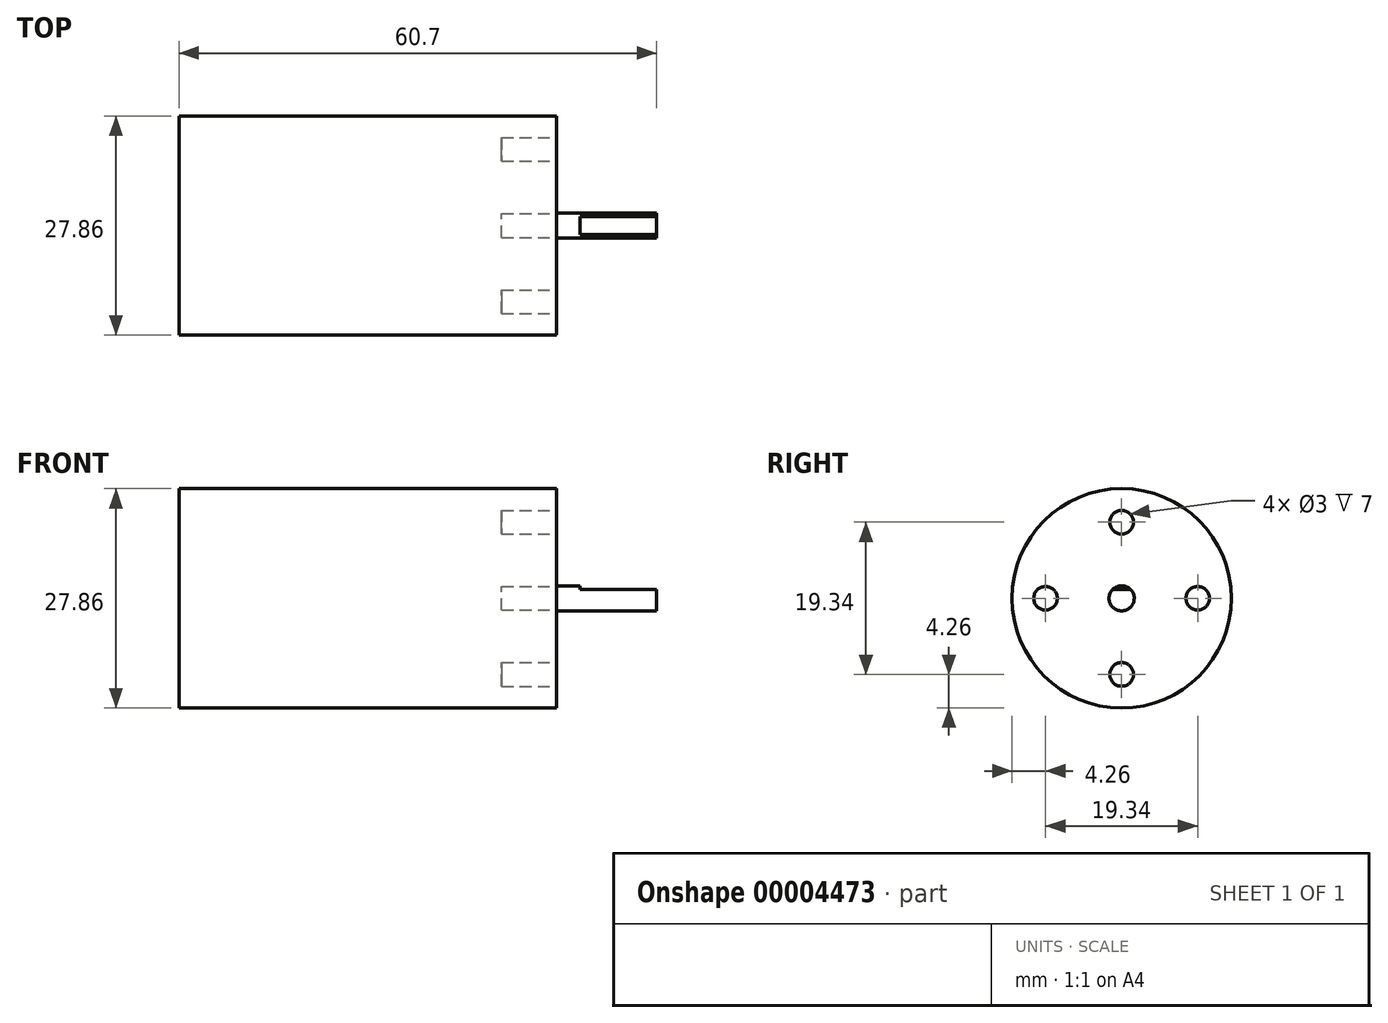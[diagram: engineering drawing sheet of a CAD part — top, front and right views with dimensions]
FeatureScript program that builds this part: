
annotation { "Feature Type Name" : "Feature", "Feature Type Description" : "" }
export const myFeature = defineFeature(function(context is Context, id is Id, definition is map)
    precondition{}
    {
        {
            var Q0;
            Q0=qCreatedBy(makeId("Front.planeOp"),FACE);
            var sketch = newSketch(context, id + "F0", { "sketchPlane" : qUnion([Q0])});
            skLineSegment(sketch, "E0", {"start": v(-48, 0) * mm, "end": v(-48, 13.93) * mm});
            skLineSegment(sketch, "E1", {"start": v(-48, 13.93) * mm, "end": v(0, 13.93) * mm});
            skLineSegment(sketch, "E2", {"start": v(0, 13.93) * mm, "end": v(0, 0) * mm});
            skLineSegment(sketch, "E3", {"start": v(0, 1.6) * mm, "end": v(12.7, 1.6) * mm});
            skLineSegment(sketch, "E4", {"start": v(12.7, 1.6) * mm, "end": v(12.7, 0) * mm});
            skLineSegment(sketch, "E5", {"start": v(2.98, 1.6) * mm, "end": v(2.98, 1.12) * mm});
            skLineSegment(sketch, "E6", {"start": v(2.98, 1.12) * mm, "end": v(12.7, 1.12) * mm});
            skLineSegment(sketch, "E7", {"start": v(-62.12, 0) * mm, "end": v(33.72, 0) * mm, "construction": true});
            skLineSegment(sketch, "E8", {"start": v(-48, 0) * mm, "end": v(12.7, 0) * mm});
            skSolve(sketch);
        }
        {
            var Q0;
            Q0=qCreatedBy(makeId("Right.planeOp"),FACE);
            var sketch = newSketch(context, id + "F1", { "sketchPlane" : qUnion([Q0])});
            skLineSegment(sketch, "E9", {"start": v(0, 0) * mm, "end": v(9.67, 0) * mm});
            skCircle(sketch, "E10", {"center": v(9.67, 0) * mm, "radius": 1.5 * mm});
            skSolve(sketch);
        }
        {
            var Q0;
            {var subQ3=sQuery(id+"F0.wireOp",EDGE,"E0");Q0=makeQuery(id+"F0.imprint","IMPRINT",FACE,{"disambiguationData":[TD([[makeQuery(id+"F0.imprint","IMPRINT",EDGE,{"derivedFrom":subQ3}),-1.0]])]});}
            var Q1;
            {var subQ6=sQuery(id+"F0.wireOp",EDGE,"E5");Q1=makeQuery(id+"F0.imprint","IMPRINT",FACE,{"disambiguationData":[TD([[makeQuery(id+"F0.imprint","IMPRINT",EDGE,{"derivedFrom":subQ6}),-1.0]])]});}
            var Q2;
            {var subQ1=sQuery(id+"F0.wireOp",EDGE,"E5");Q2=makeQuery(id+"F0.imprint","IMPRINT",FACE,{"disambiguationData":[TD([[makeQuery(id+"F0.imprint","IMPRINT",EDGE,{"derivedFrom":subQ1}),1.0]])]});}
            var Q3;
            Q3=sQuery(id+"F0.wireOp",EDGE,"E7");
            revolve(context, id + "F2", {"entities" : qUnion([Q0, Q1, Q2]), "axis" : qUnion([Q3]), "revolveType" : RevolveType.FULL});
        }
        {
            var Q0;
            {var subQ1=sQuery(id+"F0.wireOp",EDGE,"E5");Q0=makeQuery(id+"F0.imprint","IMPRINT",FACE,{"disambiguationData":[TD([[makeQuery(id+"F0.imprint","IMPRINT",EDGE,{"derivedFrom":subQ1}),1.0]])]});}
            extrude(context, id + "F3", {"entities" : qUnion([Q0]), "operationType" : NewBodyOperationType.REMOVE, "endBound" : BoundingType.SYMMETRIC, "oppositeDirection" : true, "depth" : 10 * mm});
        }
        {
            var Q0;
            {var subQ0=sQuery(id+"F1.wireOp",EDGE,"E10");Q0=makeQuery(id+"F1.imprint","IMPRINT",FACE,{"disambiguationData":[TD([[makeQuery(id+"F1.imprint","IMPRINT",EDGE,{"derivedFrom":subQ0}),1.0]])]});}
            extrude(context, id + "F4", {"entities" : qUnion([Q0]), "oppositeDirection" : true, "depth" : 7 * mm});
        }
        {
            var Q0;
            Q0=makeQuery(id+"F4.opExtrude","SWEPT_BODY",BODY,{"disambiguationData":[OSD([sQuery(id+"F1.wireOp",EDGE,"E10")])]});
            var Q1;
            Q1=sQuery(id+"F0.wireOp",EDGE,"E7");
            circularPattern(context, id + "F5", {"entities" : qUnion([Q0]), "axis" : qUnion([Q1]), "angle" : 90 * degree, "instanceCount" : 4});
        }
        {
            var Q0;
            Q0=makeQuery(id+"F5.opPattern","COPY",BODY,{"derivedFrom":makeQuery(id+"F4.opExtrude","SWEPT_BODY",BODY,{"disambiguationData":[OSD([sQuery(id+"F1.wireOp",EDGE,"E10")])]}),"instanceName":"2"});
            var Q1;
            Q1=makeQuery(id+"F4.opExtrude","SWEPT_BODY",BODY,{"disambiguationData":[OSD([sQuery(id+"F1.wireOp",EDGE,"E10")])]});
            var Q2;
            Q2=makeQuery(id+"F5.opPattern","COPY",BODY,{"derivedFrom":makeQuery(id+"F4.opExtrude","SWEPT_BODY",BODY,{"disambiguationData":[OSD([sQuery(id+"F1.wireOp",EDGE,"E10")])]}),"instanceName":"1"});
            var Q3;
            Q3=makeQuery(id+"F5.opPattern","COPY",BODY,{"derivedFrom":makeQuery(id+"F4.opExtrude","SWEPT_BODY",BODY,{"disambiguationData":[OSD([sQuery(id+"F1.wireOp",EDGE,"E10")])]}),"instanceName":"3"});
            var Q4;
            Q4=makeQuery(id+"F2.opRevolve","SWEPT_BODY",BODY,{"disambiguationData":[OSD([sQuery(id+"F0.wireOp",EDGE,"E0"),sQuery(id+"F0.wireOp",EDGE,"E1"),sQuery(id+"F0.wireOp",EDGE,"E2"),sQuery(id+"F0.wireOp",EDGE,"E3"),sQuery(id+"F0.wireOp",EDGE,"E4"),sQuery(id+"F0.wireOp",EDGE,"E8")])]});
            booleanBodies(context, id + "F6", {"operationType" : BooleanOperationType.SUBTRACTION, "tools" : qUnion([Q0, Q1, Q2, Q3]), "targets" : qUnion([Q4])});
        }
    });
